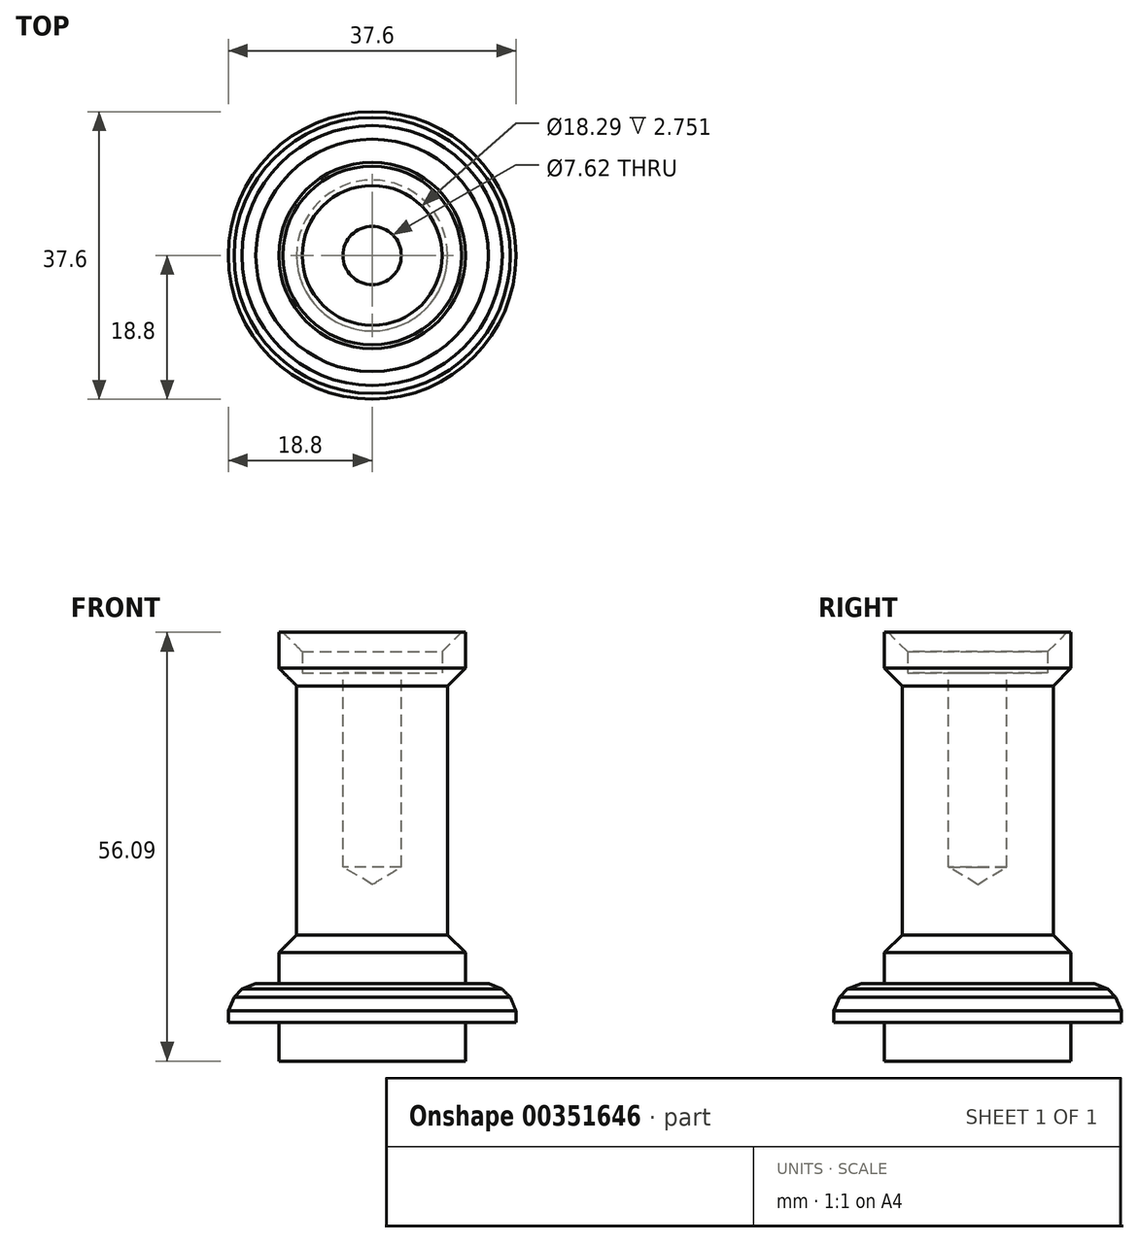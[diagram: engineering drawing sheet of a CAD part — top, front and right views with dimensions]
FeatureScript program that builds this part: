
annotation { "Feature Type Name" : "Feature", "Feature Type Description" : "" }
export const myFeature = defineFeature(function(context is Context, id is Id, definition is map)
    precondition{}
    {
        {
            var Q0;
            Q0=qCreatedBy(makeId("Front.planeOp"),FACE);
            var sketch = newSketch(context, id + "F0", { "sketchPlane" : qUnion([Q0])});
            skLineSegment(sketch, "E0", {"start": v(0, 0) * mm, "end": v(12.2, 0) * mm});
            skLineSegment(sketch, "E1", {"start": v(0, 0) * mm, "end": v(0, 50.8) * mm});
            skLineSegment(sketch, "E2", {"start": v(0, 50.8) * mm, "end": v(12.2, 50.8) * mm});
            skLineSegment(sketch, "E3", {"start": v(12.2, 50.8) * mm, "end": v(12.2, 0) * mm});
            skLineSegment(sketch, "E4.bottom", {"start": v(6.1, 50.8) * mm, "end": v(12.2, 50.8) * mm});
            skLineSegment(sketch, "E4.top", {"start": v(9.14, 56.1) * mm, "end": v(12.2, 56.1) * mm});
            skLineSegment(sketch, "E4.right", {"start": v(12.2, 50.8) * mm, "end": v(12.2, 56.1) * mm});
            skLineSegment(sketch, "E5.bottom", {"start": v(9.14, 50.8) * mm, "end": v(12.2, 50.8) * mm});
            skLineSegment(sketch, "E5.left", {"start": v(9.14, 50.8) * mm, "end": v(9.14, 56.1) * mm});
            skLineSegment(sketch, "E6", {"start": v(6.1, 50.8) * mm, "end": v(0, 47.48) * mm});
            skLineSegment(sketch, "E7", {"start": v(6.1, 0) * mm, "end": v(6.1, 5.08) * mm});
            skLineSegment(sketch, "E8.bottom", {"start": v(6.1, 5.08) * mm, "end": v(18.8, 5.08) * mm});
            skLineSegment(sketch, "E8.top", {"start": v(6.1, 0) * mm, "end": v(12.2, 0) * mm});
            skLineSegment(sketch, "E8.left", {"start": v(6.1, 5.08) * mm, "end": v(6.1, 0) * mm});
            skLineSegment(sketch, "E9.bottom", {"start": v(18.8, 5.08) * mm, "end": v(6.1, 5.08) * mm});
            skLineSegment(sketch, "E9.top", {"start": v(18.8, 10.16) * mm, "end": v(6.1, 10.16) * mm});
            skLineSegment(sketch, "E9.left", {"start": v(18.8, 5.08) * mm, "end": v(18.8, 10.16) * mm});
            skLineSegment(sketch, "E9.right", {"start": v(6.1, 5.08) * mm, "end": v(6.1, 10.16) * mm});
            skPoint(sketch, "E8.right.end.orphan", {"position": v(18.8, 0) * mm});
            skSolve(sketch);
        }
        {
            var Q0;
            {var subQ6=sQuery(id+"F0.wireOp",EDGE,"E9.left");var subQ16=sQuery(id+"F0.wireOp",EDGE,"E6");var subQ18=makeQuery(id+"F0.imprint","IMPRINT",EDGE,{"derivedFrom":subQ16});var subQ20=sQuery(id+"F0.wireOp",EDGE,"E7");var subQ22=sQuery(id+"F0.wireOp",EDGE,"E9.right");var subQ24=makeQuery(id+"F0.imprint","IMPRINT",EDGE,{"derivedFrom":subQ20});var subQ25=makeQuery(id+"F0.imprint","IMPRINT",EDGE,{"derivedFrom":subQ22});Q0=qUnion([makeQuery(id+"F0.imprint","IMPRINT",FACE,{"disambiguationData":[TD([[subQ24,-1.0]])]}),makeQuery(id+"F0.imprint","IMPRINT",FACE,{"disambiguationData":[TD([[subQ18,-1.0]])]}),makeQuery(id+"F0.imprint","IMPRINT",FACE,{"disambiguationData":[TD([[subQ25,-1.0]])]}),makeQuery(id+"F0.imprint","IMPRINT",FACE,{"disambiguationData":[TD([[makeQuery(id+"F0.imprint","IMPRINT",EDGE,{"derivedFrom":sQuery(id+"F0.wireOp",EDGE,"E4.top")}),-1.0]])]}),makeQuery(id+"F0.imprint","IMPRINT",FACE,{"disambiguationData":[TD([[subQ18,1.0]])]}),makeQuery(id+"F0.imprint","IMPRINT",FACE,{"disambiguationData":[TD([[makeQuery(id+"F0.imprint","IMPRINT",EDGE,{"derivedFrom":subQ6}),1.0]])]})]);}
            var Q1;
            Q1=sQuery(id+"F0.wireOp",EDGE,"E1");
            revolve(context, id + "F1", {"entities" : qUnion([Q0]), "axis" : qUnion([Q1]), "revolveType" : RevolveType.FULL});
        }
        {
            var Q0;
            Q0=makeQuery(id+"F1.opRevolve","SWEPT_EDGE",EDGE,{"disambiguationData":[OSD([sQuery(id+"F0.wireOp",EDGE,"E4.top"),sQuery(id+"F0.wireOp",EDGE,"E5.left")])]});
            chamfer(context, id + "F2", {"entities" : qUnion([Q0]), "width" : 2.54 * mm, "tangentPropagation" : true});
        }
        {
            var Q0;
            Q0=makeQuery(id+"F1.opRevolve","SWEPT_EDGE",EDGE,{"disambiguationData":[OSD([sQuery(id+"F0.wireOp",EDGE,"E9.top"),sQuery(id+"F0.wireOp",EDGE,"E9.left")])]});
            chamfer(context, id + "F3", {"entities" : qUnion([Q0]), "width" : 2.54 * mm, "tangentPropagation" : true});
        }
        {
            var Q0;
            Q0=makeQuery(id+"F1.opRevolve","SWEPT_FACE",FACE,{"disambiguationData":[OSD([sQuery(id+"F0.wireOp",EDGE,"E2")])]});
            var sketch = newSketch(context, id + "F4", { "sketchPlane" : qUnion([Q0])});
            skPoint(sketch, "E10", {"position": v(0, 0) * mm});
            skSolve(sketch);
        }
        {
            var Q0;
            Q0=sQuery(id+"F4.wireOp",VERTEX,"E10");
            var Q1;
            Q1=makeQuery(id+"F1.opRevolve","SWEPT_BODY",BODY,{"disambiguationData":[OSD([sQuery(id+"F0.wireOp",EDGE,"E0"),sQuery(id+"F0.wireOp",EDGE,"E1"),sQuery(id+"F0.wireOp",EDGE,"E2"),sQuery(id+"F0.wireOp",EDGE,"E3"),sQuery(id+"F0.wireOp",EDGE,"E4.top"),sQuery(id+"F0.wireOp",EDGE,"E4.right"),sQuery(id+"F0.wireOp",EDGE,"E5.left"),sQuery(id+"F0.wireOp",EDGE,"E8.bottom"),sQuery(id+"F0.wireOp",EDGE,"E9.top"),sQuery(id+"F0.wireOp",EDGE,"E9.left")])]});
            hole(context, id + "F5", {"style" : HoleStyle.SIMPLE, "endStyle" : HoleEndStyle.BLIND, "holeDiameter" : 7.62 * mm, "holeDepth" : 25.4 * mm, "isTappedThrough" : true, "tappedDepth" : 12.7 * mm, "tapClearance" : 3, "locations" : qUnion([Q0]), "scope" : qUnion([Q1])});
        }
        {
            var Q0;
            Q0=qCreatedBy(makeId("Right.planeOp"),FACE);
            var sketch = newSketch(context, id + "F6", { "sketchPlane" : qUnion([Q0])});
            skLineSegment(sketch, "E11", {"start": v(0, 50.9) * mm, "end": v(0, 20.96) * mm});
            skLineSegment(sketch, "E12.bottom", {"start": v(0, 48.86) * mm, "end": v(-9.87, 48.86) * mm});
            skLineSegment(sketch, "E12.top", {"start": v(0, 16.73) * mm, "end": v(-9.87, 16.73) * mm});
            skLineSegment(sketch, "E12.left", {"start": v(0, 48.86) * mm, "end": v(0, 16.73) * mm});
            skLineSegment(sketch, "E12.right", {"start": v(-9.87, 48.86) * mm, "end": v(-9.87, 16.73) * mm});
            skLineSegment(sketch, "E13.bottom", {"start": v(-9.87, 48.86) * mm, "end": v(-17.15, 48.86) * mm});
            skLineSegment(sketch, "E13.top", {"start": v(-9.87, 16.73) * mm, "end": v(-17.15, 16.73) * mm});
            skLineSegment(sketch, "E13.right", {"start": v(-17.15, 48.86) * mm, "end": v(-17.15, 16.73) * mm});
            skSolve(sketch);
        }
        {
            var Q0;
            Q0=makeQuery(id+"F6.imprint","IMPRINT",FACE,{"disambiguationData":[TD([[makeQuery(id+"F6.imprint","IMPRINT",EDGE,{"derivedFrom":sQuery(id+"F6.wireOp",EDGE,"E13.bottom")}),1.0]])]});
            var Q1;
            Q1=sQuery(id+"F6.wireOp",EDGE,"E12.left");
            revolve(context, id + "F7", {"operationType" : NewBodyOperationType.REMOVE, "entities" : qUnion([Q0]), "axis" : qUnion([Q1]), "revolveType" : RevolveType.FULL, "oppositeDirection" : true});
        }
        {
            var Q0;
            Q0=makeQuery(id+"F7.boolean.opBoolean","INTERSECT",EDGE,{"derivedFrom":[makeQuery(id+"F1.opRevolve","SWEPT_FACE",FACE,{"disambiguationData":[OSD([sQuery(id+"F0.wireOp",EDGE,"E3"),sQuery(id+"F0.wireOp",EDGE,"E4.right")])]}),makeQuery(id+"F7.opRevolve","SWEPT_FACE",FACE,{"disambiguationData":[OSD([sQuery(id+"F6.wireOp",EDGE,"E13.bottom")])]})]});
            var Q1;
            Q1=makeQuery(id+"F7.boolean.opBoolean","INTERSECT",EDGE,{"derivedFrom":[makeQuery(id+"F1.opRevolve","SWEPT_FACE",FACE,{"disambiguationData":[OSD([sQuery(id+"F0.wireOp",EDGE,"E3"),sQuery(id+"F0.wireOp",EDGE,"E4.right")])]}),makeQuery(id+"F7.opRevolve","SWEPT_FACE",FACE,{"disambiguationData":[OSD([sQuery(id+"F6.wireOp",EDGE,"E13.top")])]})]});
            var Q2;
            {var subQ0=sQuery(id+"F0.wireOp",EDGE,"E9.top");Q2=makeQuery(id+"F3.opChamfer","BLEND_EDGE",EDGE,{"blendedFrom":[makeQuery(id+"F1.opRevolve","SWEPT_EDGE",EDGE,{"disambiguationData":[OSD([subQ0,sQuery(id+"F0.wireOp",EDGE,"E9.left")])]}),makeQuery(id+"F1.opRevolve","SWEPT_FACE",FACE,{"disambiguationData":[OSD([subQ0])]})],"blendedInto":[makeQuery(id+"F1.opRevolve","SWEPT_FACE",FACE,{"disambiguationData":[OSD([subQ0])]})]});}
            var Q3;
            {var subQ0=sQuery(id+"F0.wireOp",EDGE,"E9.left");Q3=makeQuery(id+"F3.opChamfer","BLEND_EDGE",EDGE,{"blendedFrom":[makeQuery(id+"F1.opRevolve","SWEPT_EDGE",EDGE,{"disambiguationData":[OSD([sQuery(id+"F0.wireOp",EDGE,"E9.top"),subQ0])]}),makeQuery(id+"F1.opRevolve","SWEPT_FACE",FACE,{"disambiguationData":[OSD([subQ0])]})],"blendedInto":[makeQuery(id+"F1.opRevolve","SWEPT_FACE",FACE,{"disambiguationData":[OSD([subQ0])]})]});}
            var Q4;
            Q4=makeQuery(id+"F5.hole-0.boolean.opBoolean","COPY",EDGE,{"derivedFrom":makeQuery(id+"F5.hole-0.opRevolve","SWEPT_EDGE",EDGE,{"disambiguationData":[OSD([sQuery(id+"F5.hole-0.sketch.wireOp",EDGE,"core_line_2"),sQuery(id+"F5.hole-0.sketch.wireOp",EDGE,"core_line_3")])]})});
            chamfer(context, id + "F8", {"entities" : qUnion([Q0, Q1, Q2, Q3, Q4]), "width" : 2.54 * mm, "tangentPropagation" : true});
        }
    });
